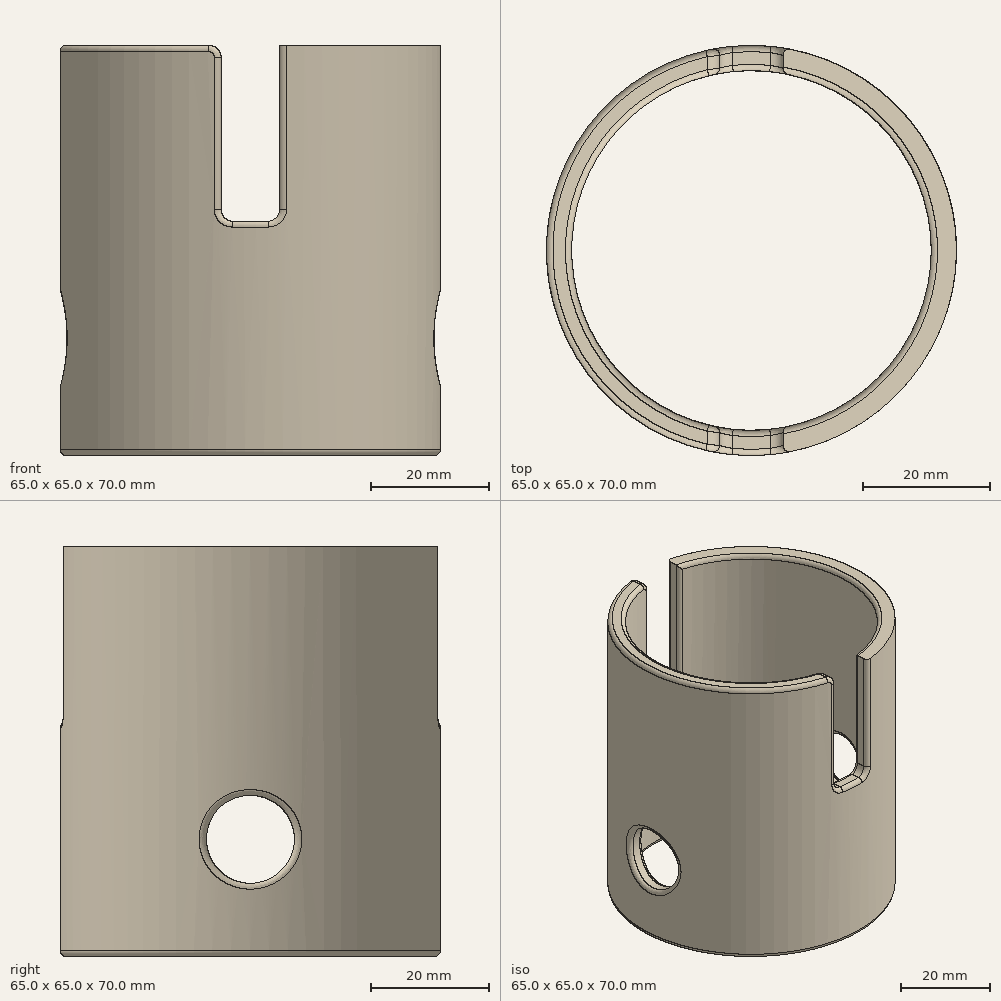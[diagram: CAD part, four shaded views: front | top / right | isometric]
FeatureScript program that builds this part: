
annotation { "Feature Type Name" : "Feature", "Feature Type Description" : "" }
export const myFeature = defineFeature(function(context is Context, id is Id, definition is map)
    precondition{}
    {
        {
            var Q0;
            Q0=qCreatedBy(makeId("Top.planeOp"),FACE);
            var sketch = newSketch(context, id + "F0", { "sketchPlane" : qUnion([Q0])});
            skPoint(sketch, "E0", {"position": v(0, 0) * mm});
            skCircle(sketch, "E1", {"center": v(0, 0) * mm, "radius": 32.5 * mm});
            skSolve(sketch);
        }
        {
            var Q0;
            Q0 = qSketchRegion(id + "F0", true);
            extrude(context, id + "F1", {"entities" : qUnion([Q0]), "oppositeDirection" : true, "depth" : 70 * mm});
        }
        {
            var Q0;
            Q0=makeQuery(id+"F0.imprint","IMPRINT",FACE,{"disambiguationData":[TD([[makeQuery(id+"F0.imprint","IMPRINT",EDGE,{"derivedFrom":sQuery(id+"F0.wireOp",EDGE,"E1")}),1.0]])]});
            var sketch = newSketch(context, id + "F2", { "sketchPlane" : qUnion([Q0])});
            skCircle(sketch, "E2.0", {"center": v(0, 0) * mm, "radius": 28.5 * mm});
            skSolve(sketch);
        }
        {
            var Q0;
            Q0=makeQuery(id+"F2.imprint","IMPRINT",FACE,{"disambiguationData":[TD([[makeQuery(id+"F2.imprint","IMPRINT",EDGE,{"derivedFrom":sQuery(id+"F2.wireOp",EDGE,"E2.0")}),1.0]])]});
            var Q1;
            Q1=sQuery(id+"F2.wireOp",EDGE,"E2.0");
            extrude(context, id + "F3", {"entities" : qUnion([Q0]), "operationType" : NewBodyOperationType.REMOVE, "surfaceEntities" : qUnion([Q1]), "endBound" : BoundingType.THROUGH_ALL, "oppositeDirection" : true, "depth" : 25 * mm});
        }
        {
            var Q0;
            Q0=qCreatedBy(makeId("Top.planeOp"),FACE);
            var sketch = newSketch(context, id + "F4", { "sketchPlane" : qUnion([Q0])});
            skLineSegment(sketch, "E3.bottom", {"start": v(5, -35) * mm, "end": v(-5, -35) * mm});
            skLineSegment(sketch, "E3.top", {"start": v(5, 35) * mm, "end": v(-5, 35) * mm});
            skLineSegment(sketch, "E3.left", {"start": v(5, -35) * mm, "end": v(5, 35) * mm});
            skLineSegment(sketch, "E3.right", {"start": v(-5, -35) * mm, "end": v(-5, 35) * mm});
            skPoint(sketch, "E3.middle", {"position": v(0, 0) * mm});
            skSolve(sketch);
        }
        {
            var Q0;
            Q0=makeQuery(id+"F4.imprint","IMPRINT",FACE,{"disambiguationData":[TD([[makeQuery(id+"F4.imprint","IMPRINT",EDGE,{"derivedFrom":sQuery(id+"F4.wireOp",EDGE,"E3.bottom")}),-1.0]])]});
            extrude(context, id + "F5", {"entities" : qUnion([Q0]), "operationType" : NewBodyOperationType.REMOVE, "oppositeDirection" : true, "depth" : 30 * mm});
        }
        {
            var Q0;
            Q0=qCreatedBy(makeId("Right.planeOp"),FACE);
            var sketch = newSketch(context, id + "F6", { "sketchPlane" : qUnion([Q0])});
            skLineSegment(sketch, "E4", {"start": v(-40.2, -50) * mm, "end": v(39.44, -50) * mm});
            skPoint(sketch, "E5", {"position": v(0, -50) * mm});
            skCircle(sketch, "E6", {"center": v(0, -50) * mm, "radius": 7.5 * mm});
            skSolve(sketch);
        }
        {
            var Q0;
            Q0 = qSketchRegion(id + "F6", true);
            extrude(context, id + "F7", {"entities" : qUnion([Q0]), "operationType" : NewBodyOperationType.REMOVE, "endBound" : BoundingType.THROUGH_ALL, "depth" : 25 * mm, "hasSecondDirection" : true, "secondDirectionBound" : SecondDirectionBoundingType.THROUGH_ALL, "secondDirectionOppositeDirection" : true, "secondDirectionDepth" : 25 * mm});
        }
        {
            var Q0;
            Q0=makeQuery(id+"F5.boolean.opBoolean","COPY",EDGE,{"disambiguationData":[OD(0.0)],"derivedFrom":makeQuery(id+"F5.opExtrude","CAP_EDGE",EDGE,{"disambiguationData":[OSD([sQuery(id+"F4.wireOp",EDGE,"E3.right")])],"isStart":true})});
            var Q1;
            Q1=makeQuery(id+"F5.boolean.opBoolean","COPY",EDGE,{"disambiguationData":[OD(0.0)],"derivedFrom":makeQuery(id+"F5.opExtrude","CAP_EDGE",EDGE,{"disambiguationData":[OSD([sQuery(id+"F4.wireOp",EDGE,"E3.left")])],"isStart":true})});
            var Q2;
            Q2=makeQuery(id+"F5.boolean.opBoolean","COPY",EDGE,{"disambiguationData":[OD(1.0)],"derivedFrom":makeQuery(id+"F5.opExtrude","CAP_EDGE",EDGE,{"disambiguationData":[OSD([sQuery(id+"F4.wireOp",EDGE,"E3.left")])],"isStart":true})});
            var Q3;
            Q3=makeQuery(id+"F5.boolean.opBoolean","COPY",EDGE,{"disambiguationData":[OD(1.0)],"derivedFrom":makeQuery(id+"F5.opExtrude","CAP_EDGE",EDGE,{"disambiguationData":[OSD([sQuery(id+"F4.wireOp",EDGE,"E3.right")])],"isStart":true})});
            var Q4;
            Q4=makeQuery(id+"F5.boolean.opBoolean","COPY",EDGE,{"disambiguationData":[OD(0.0)],"derivedFrom":makeQuery(id+"F5.opExtrude","CAP_EDGE",EDGE,{"disambiguationData":[OSD([sQuery(id+"F4.wireOp",EDGE,"E3.right")])],"isStart":false})});
            var Q5;
            Q5=makeQuery(id+"F5.boolean.opBoolean","COPY",EDGE,{"disambiguationData":[OD(0.0)],"derivedFrom":makeQuery(id+"F5.opExtrude","CAP_EDGE",EDGE,{"disambiguationData":[OSD([sQuery(id+"F4.wireOp",EDGE,"E3.left")])],"isStart":false})});
            var Q6;
            Q6=makeQuery(id+"F5.boolean.opBoolean","COPY",EDGE,{"disambiguationData":[OD(1.0)],"derivedFrom":makeQuery(id+"F5.opExtrude","CAP_EDGE",EDGE,{"disambiguationData":[OSD([sQuery(id+"F4.wireOp",EDGE,"E3.right")])],"isStart":false})});
            var Q7;
            Q7=makeQuery(id+"F5.boolean.opBoolean","COPY",EDGE,{"disambiguationData":[OD(1.0)],"derivedFrom":makeQuery(id+"F5.opExtrude","CAP_EDGE",EDGE,{"disambiguationData":[OSD([sQuery(id+"F4.wireOp",EDGE,"E3.left")])],"isStart":false})});
            fillet(context, id + "F8", {"entities" : qUnion([Q0, Q1, Q2, Q3, Q4, Q5, Q6, Q7]), "radius" : 2 * mm, "tangentPropagation" : true, "allowEdgeOverflow" : false});
        }
        {
            var Q0;
            Q0=makeQuery(id+"F7.boolean.opBoolean","INTERSECT",EDGE,{"disambiguationData":[OD(0.0)],"derivedFrom":[makeQuery(id+"F1.opExtrude","SWEPT_FACE",FACE,{"disambiguationData":[OSD([sQuery(id+"F0.wireOp",EDGE,"E1")])]}),makeQuery(id+"F7.opExtrude","SWEPT_FACE",FACE,{"disambiguationData":[OSD([sQuery(id+"F6.wireOp",EDGE,"E6")])]})]});
            var Q1;
            Q1=makeQuery(id+"F7.boolean.opBoolean","INTERSECT",EDGE,{"disambiguationData":[OD(1.0)],"derivedFrom":[makeQuery(id+"F1.opExtrude","SWEPT_FACE",FACE,{"disambiguationData":[OSD([sQuery(id+"F0.wireOp",EDGE,"E1")])]}),makeQuery(id+"F7.opExtrude","SWEPT_FACE",FACE,{"disambiguationData":[OSD([sQuery(id+"F6.wireOp",EDGE,"E6")])]})]});
            var Q2;
            Q2=makeQuery(id+"F7.boolean.opBoolean","INTERSECT",EDGE,{"disambiguationData":[OD(1.0)],"derivedFrom":[makeQuery(id+"F3.boolean.opBoolean","COPY",FACE,{"derivedFrom":makeQuery(id+"F3.opExtrude","SWEPT_FACE",FACE,{"disambiguationData":[OSD([sQuery(id+"F2.wireOp",EDGE,"E2.0")])]})}),makeQuery(id+"F7.opExtrude","SWEPT_FACE",FACE,{"disambiguationData":[OSD([sQuery(id+"F6.wireOp",EDGE,"E6")])]})]});
            var Q3;
            Q3=makeQuery(id+"F7.boolean.opBoolean","INTERSECT",EDGE,{"disambiguationData":[OD(0.0)],"derivedFrom":[makeQuery(id+"F3.boolean.opBoolean","COPY",FACE,{"derivedFrom":makeQuery(id+"F3.opExtrude","SWEPT_FACE",FACE,{"disambiguationData":[OSD([sQuery(id+"F2.wireOp",EDGE,"E2.0")])]})}),makeQuery(id+"F7.opExtrude","SWEPT_FACE",FACE,{"disambiguationData":[OSD([sQuery(id+"F6.wireOp",EDGE,"E6")])]})]});
            fillet(context, id + "F9", {"entities" : qUnion([Q0, Q1, Q2, Q3]), "radius" : 1 * mm, "tangentPropagation" : true, "allowEdgeOverflow" : false});
        }
        {
            var Q0;
            Q0=makeQuery(id+"F3.boolean.opBoolean","COPY",FACE,{"derivedFrom":makeQuery(id+"F3.opExtrude","SWEPT_FACE",FACE,{"disambiguationData":[OSD([sQuery(id+"F2.wireOp",EDGE,"E2.0")])]})});
            fillet(context, id + "F10", {"entities" : qUnion([Q0]), "radius" : 1 * mm, "tangentPropagation" : true, "allowEdgeOverflow" : false});
        }
        {
            var Q0;
            {var subQ0=sQuery(id+"F0.wireOp",EDGE,"E1");Q0=makeQuery(id+"F5.boolean.opBoolean","SPLIT",EDGE,{"disambiguationData":[TD([makeQuery(id+"F5.opExtrude","SWEPT_FACE",FACE,{"disambiguationData":[OSD([sQuery(id+"F4.wireOp",EDGE,"E3.right")])]})])],"derivedFrom":makeQuery(id+"F1.opExtrude","CAP_EDGE",EDGE,{"disambiguationData":[OSD([subQ0])],"isStart":true})});}
            fillet(context, id + "F11", {"entities" : qUnion([Q0]), "radius" : 1 * mm, "tangentPropagation" : true, "allowEdgeOverflow" : false});
        }
        {
            var Q0;
            Q0=makeQuery(id+"F1.opExtrude","CAP_EDGE",EDGE,{"disambiguationData":[OSD([sQuery(id+"F0.wireOp",EDGE,"E1")])],"isStart":false});
            fillet(context, id + "F12", {"entities" : qUnion([Q0]), "radius" : 1 * mm, "tangentPropagation" : true, "allowEdgeOverflow" : false});
        }
    });
